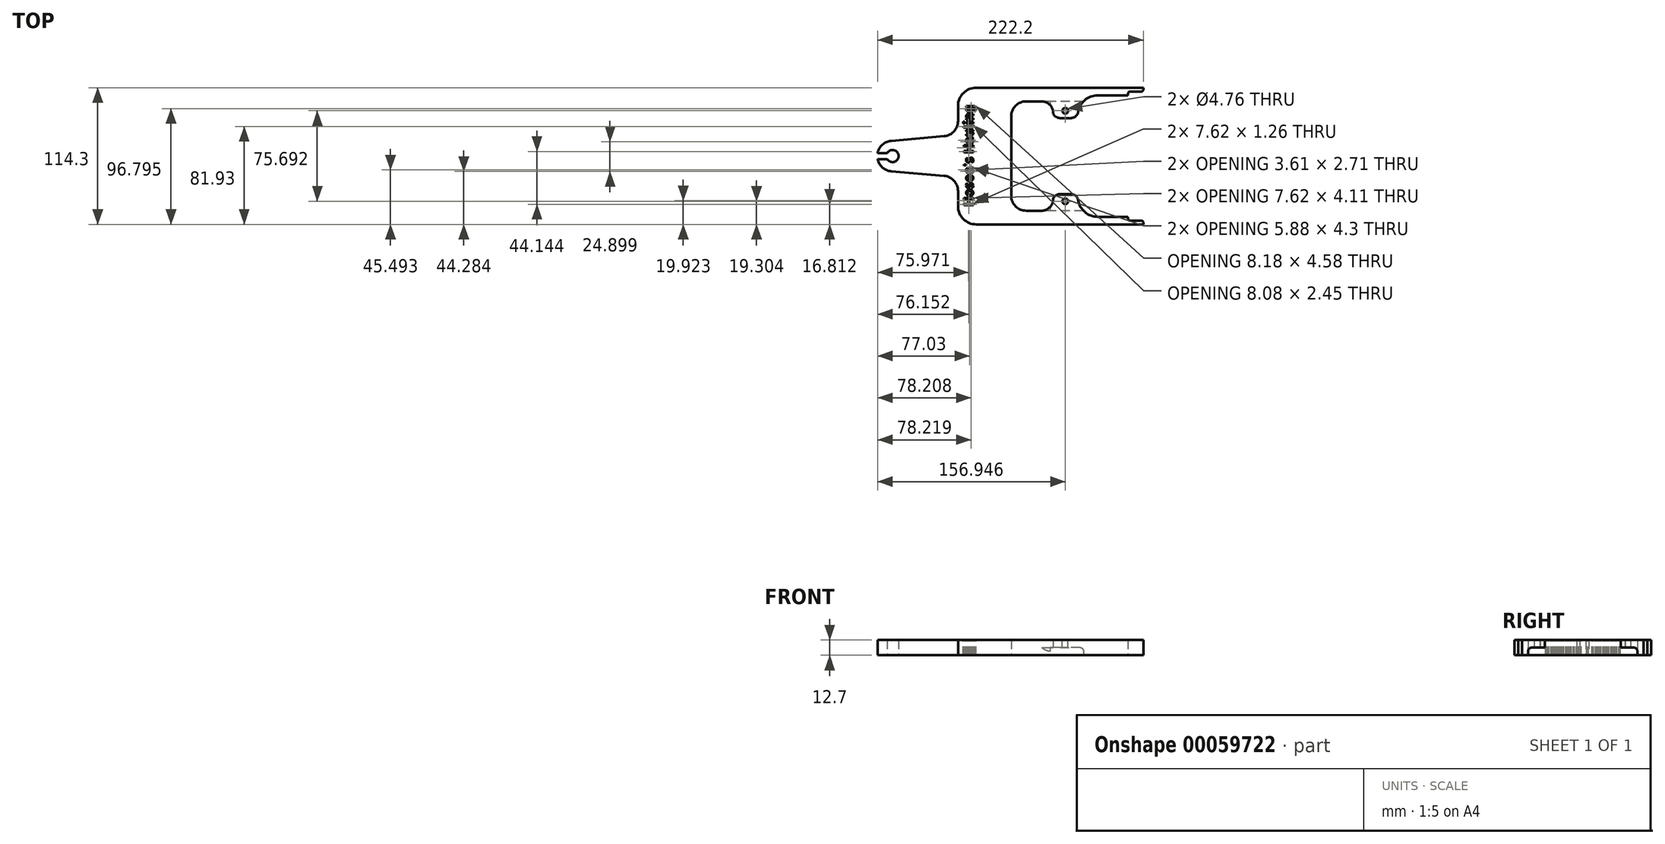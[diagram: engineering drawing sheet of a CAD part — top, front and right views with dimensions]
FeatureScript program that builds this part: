
annotation { "Feature Type Name" : "Feature", "Feature Type Description" : "" }
export const myFeature = defineFeature(function(context is Context, id is Id, definition is map)
    precondition{}
    {
        {
            var Q0;
            Q0=qCreatedBy(makeId("Top.planeOp"),FACE);
            var sketch = newSketch(context, id + "F0", { "sketchPlane" : qUnion([Q0])});
            skLineSegment(sketch, "E0", {"start": v(-226.79, 0) * mm, "end": v(91.5, 0) * mm, "construction": true});
            skLineSegment(sketch, "E1.MirrorCS", {"start": v(-31.43, 31.75) * mm, "end": v(-22.54, 31.75) * mm});
            skLineSegment(sketch, "E2", {"start": v(-116.84, 41.9) * mm, "end": v(-116.84, 29.23) * mm});
            skLineSegment(sketch, "E3", {"start": v(-128.43, 16.57) * mm, "end": v(-172.71, 12.7) * mm});
            skArc(sketch, "E4", {"start": v(-101.6, 57.15) * mm, "mid": v(-112.38, 52.69) * mm, "end": v(-116.84, 41.9) * mm});
            skArc(sketch, "E5.filletArc", {"start": v(-128.43, 16.57) * mm, "mid": v(-120.18, 20.65) * mm, "end": v(-116.84, 29.23) * mm});
            skArc(sketch, "E6.MirrorCS", {"start": v(-101.6, -57.15) * mm, "mid": v(-112.38, -52.69) * mm, "end": v(-116.84, -41.9) * mm});
            skLineSegment(sketch, "E7.MirrorCS", {"start": v(-116.84, -41.9) * mm, "end": v(-116.84, -29.23) * mm});
            skArc(sketch, "E8.MirrorCS", {"start": v(-128.43, -16.57) * mm, "mid": v(-120.18, -20.65) * mm, "end": v(-116.84, -29.23) * mm});
            skLineSegment(sketch, "E9.MirrorCS", {"start": v(-128.43, -16.57) * mm, "end": v(-172.71, -12.7) * mm});
            skArc(sketch, "E10", {"start": v(-172.71, 12.7) * mm, "mid": v(-180.1, 9.51) * mm, "end": v(-184.1, 2.54) * mm});
            skArc(sketch, "E11.filletArc", {"start": v(-37.25, 35.56) * mm, "mid": v(-34.9, 32.79) * mm, "end": v(-31.43, 31.75) * mm});
            skArc(sketch, "E12.filletArc", {"start": v(-22.54, 31.75) * mm, "mid": v(-18.44, 33.25) * mm, "end": v(-16.28, 37.04) * mm});
            skArc(sketch, "E13", {"start": v(0, 50.8) * mm, "mid": v(-10.66, 46.9) * mm, "end": v(-16.28, 37.04) * mm});
            skLineSegment(sketch, "E14", {"start": v(-101.6, 57.15) * mm, "end": v(38.1, 57.15) * mm});
            skLineSegment(sketch, "E15", {"start": v(38.1, 57.15) * mm, "end": v(38.1, 55.56) * mm});
            skLineSegment(sketch, "E16", {"start": v(36.51, 53.98) * mm, "end": v(26.99, 53.98) * mm});
            skLineSegment(sketch, "E17", {"start": v(25.4, 52.39) * mm, "end": v(25.4, 50.8) * mm});
            skLineSegment(sketch, "E18", {"start": v(25.4, 50.8) * mm, "end": v(0, 50.8) * mm});
            skPoint(sketch, "E19.visualSharp", {"position": v(25.4, 53.98) * mm});
            skArc(sketch, "E19.filletArc", {"start": v(26.99, 53.98) * mm, "mid": v(25.86, 53.51) * mm, "end": v(25.4, 52.39) * mm});
            skPoint(sketch, "E20.visualSharp", {"position": v(38.1, 53.98) * mm});
            skArc(sketch, "E20.filletArc", {"start": v(36.51, 53.98) * mm, "mid": v(37.64, 54.44) * mm, "end": v(38.1, 55.56) * mm});
            skLineSegment(sketch, "E21", {"start": v(-72.4, 33.02) * mm, "end": v(-72.4, 0) * mm});
            skLineSegment(sketch, "E22", {"start": v(-184.1, 2.54) * mm, "end": v(-176, 2.54) * mm});
            skLineSegment(sketch, "E23", {"start": v(-184.1, -2.54) * mm, "end": v(-176, -2.54) * mm});
            skArc(sketch, "E24", {"start": v(-176, -2.54) * mm, "mid": v(-166.52, 0) * mm, "end": v(-176, 2.54) * mm});
            skArc(sketch, "E25.trimOffspring", {"start": v(-184.1, -2.54) * mm, "mid": v(-180.1, -9.51) * mm, "end": v(-172.71, -12.7) * mm});
            skLineSegment(sketch, "E26", {"start": v(-47, 45.72) * mm, "end": v(-59.7, 45.72) * mm});
            skArc(sketch, "E27", {"start": v(-37.25, 35.56) * mm, "mid": v(-39.95, 42.72) * mm, "end": v(-47, 45.72) * mm});
            skPoint(sketch, "E28.visualSharp", {"position": v(-72.4, 45.72) * mm});
            skArc(sketch, "E28.filletArc", {"start": v(-59.7, 45.72) * mm, "mid": v(-68.67, 42) * mm, "end": v(-72.4, 33.02) * mm});
            skLineSegment(sketch, "E29.MirrorCS", {"start": v(38.1, -57.15) * mm, "end": v(38.1, -55.56) * mm});
            skArc(sketch, "E30.MirrorCS", {"start": v(36.51, -53.98) * mm, "mid": v(37.64, -54.44) * mm, "end": v(38.1, -55.56) * mm});
            skArc(sketch, "E31.MirrorCS", {"start": v(26.99, -53.98) * mm, "mid": v(25.86, -53.51) * mm, "end": v(25.4, -52.39) * mm});
            skLineSegment(sketch, "E32.MirrorCS", {"start": v(25.4, -52.39) * mm, "end": v(25.4, -50.8) * mm});
            skArc(sketch, "E33.MirrorCS", {"start": v(-37.25, -35.56) * mm, "mid": v(-34.9, -32.79) * mm, "end": v(-31.43, -31.75) * mm});
            skPoint(sketch, "E34.MirrorP", {"position": v(38.1, -53.98) * mm});
            skPoint(sketch, "E35.MirrorP", {"position": v(25.4, -53.98) * mm});
            skLineSegment(sketch, "E36.MirrorCS", {"start": v(36.51, -53.98) * mm, "end": v(26.99, -53.98) * mm});
            skLineSegment(sketch, "E37.MirrorCS", {"start": v(-72.4, -33.02) * mm, "end": v(-72.4, 0) * mm});
            skLineSegment(sketch, "E38.MirrorCS", {"start": v(-47, -45.72) * mm, "end": v(-59.7, -45.72) * mm});
            skArc(sketch, "E39.MirrorCS", {"start": v(-22.54, -31.75) * mm, "mid": v(-18.44, -33.25) * mm, "end": v(-16.28, -37.04) * mm});
            skArc(sketch, "E40.MirrorCS", {"start": v(0, -50.8) * mm, "mid": v(-10.66, -46.9) * mm, "end": v(-16.28, -37.04) * mm});
            skArc(sketch, "E41.MirrorCS", {"start": v(-37.25, -35.56) * mm, "mid": v(-39.95, -42.72) * mm, "end": v(-47, -45.72) * mm});
            skLineSegment(sketch, "E42.MirrorCS", {"start": v(25.4, -50.8) * mm, "end": v(0, -50.8) * mm});
            skLineSegment(sketch, "E43.MirrorCS", {"start": v(-101.6, -57.15) * mm, "end": v(38.1, -57.15) * mm});
            skArc(sketch, "E44.MirrorCS", {"start": v(-59.7, -45.72) * mm, "mid": v(-68.67, -42) * mm, "end": v(-72.4, -33.02) * mm});
            skPoint(sketch, "E45.MirrorP", {"position": v(-72.4, -45.72) * mm});
            skLineSegment(sketch, "E46.MirrorCS", {"start": v(-31.43, -31.75) * mm, "end": v(-22.54, -31.75) * mm});
            skSolve(sketch);
        }
        {
            var Q0;
            Q0=makeQuery(id+"F0.imprint","IMPRINT",FACE,{"disambiguationData":[TD([[makeQuery(id+"F0.imprint","IMPRINT",EDGE,{"derivedFrom":sQuery(id+"F0.wireOp",EDGE,"E1.MirrorCS")}),1.0]])]});
            extrude(context, id + "F1", {"entities" : qUnion([Q0]), "depth" : 12.7 * mm});
        }
        {
            var Q0;
            Q0=makeQuery(id+"F1.opExtrude","CAP_FACE",FACE,{"disambiguationData":[OSD([sQuery(id+"F0.wireOp",EDGE,"E1.MirrorCS"),sQuery(id+"F0.wireOp",EDGE,"E2"),sQuery(id+"F0.wireOp",EDGE,"E3"),sQuery(id+"F0.wireOp",EDGE,"E4"),sQuery(id+"F0.wireOp",EDGE,"E5.filletArc"),sQuery(id+"F0.wireOp",EDGE,"E7.MirrorCS"),sQuery(id+"F0.wireOp",EDGE,"E8.MirrorCS"),sQuery(id+"F0.wireOp",EDGE,"E9.MirrorCS"),sQuery(id+"F0.wireOp",EDGE,"E10"),sQuery(id+"F0.wireOp",EDGE,"ed6b8572-d190-4678-89e8-abdbb25ba1cc"),sQuery(id+"F0.wireOp",EDGE,"E11.filletArc"),sQuery(id+"F0.wireOp",EDGE,"E12.filletArc"),sQuery(id+"F0.wireOp",EDGE,"E13"),sQuery(id+"F0.wireOp",EDGE,"E14"),sQuery(id+"F0.wireOp",EDGE,"E15"),sQuery(id+"F0.wireOp",EDGE,"E16"),sQuery(id+"F0.wireOp",EDGE,"E17"),sQuery(id+"F0.wireOp",EDGE,"E18"),sQuery(id+"F0.wireOp",EDGE,"E19.filletArc"),sQuery(id+"F0.wireOp",EDGE,"E20.filletArc"),sQuery(id+"F0.wireOp",EDGE,"E21"),sQuery(id+"F0.wireOp",EDGE,"bec62c27-19f1-4f1e-baea-a3420ca4f23a0.MirrorCS"),sQuery(id+"F0.wireOp",EDGE,"bec62c27-19f1-4f1e-baea-a3420ca4f23a1.MirrorCS"),sQuery(id+"F0.wireOp",EDGE,"bec62c27-19f1-4f1e-baea-a3420ca4f23a2.MirrorCS"),sQuery(id+"F0.wireOp",EDGE,"bec62c27-19f1-4f1e-baea-a3420ca4f23a3.MirrorCS"),sQuery(id+"F0.wireOp",EDGE,"bec62c27-19f1-4f1e-baea-a3420ca4f23a4.MirrorCS"),sQuery(id+"F0.wireOp",EDGE,"E6.MirrorCS"),sQuery(id+"F0.wireOp",EDGE,"bec62c27-19f1-4f1e-baea-a3420ca4f23a7.MirrorCS"),sQuery(id+"F0.wireOp",EDGE,"bec62c27-19f1-4f1e-baea-a3420ca4f23a8.MirrorCS"),sQuery(id+"F0.wireOp",EDGE,"bec62c27-19f1-4f1e-baea-a3420ca4f23a9.MirrorCS"),sQuery(id+"F0.wireOp",EDGE,"bec62c27-19f1-4f1e-baea-a3420ca4f23a10.MirrorCS"),sQuery(id+"F0.wireOp",EDGE,"bec62c27-19f1-4f1e-baea-a3420ca4f23a11.MirrorCS"),sQuery(id+"F0.wireOp",EDGE,"bec62c27-19f1-4f1e-baea-a3420ca4f23a12.MirrorCS"),sQuery(id+"F0.wireOp",EDGE,"bec62c27-19f1-4f1e-baea-a3420ca4f23a14.MirrorCS"),sQuery(id+"F0.wireOp",EDGE,"bec62c27-19f1-4f1e-baea-a3420ca4f23a15.MirrorCS"),sQuery(id+"F0.wireOp",EDGE,"E22"),sQuery(id+"F0.wireOp",EDGE,"E23"),sQuery(id+"F0.wireOp",EDGE,"E24"),sQuery(id+"F0.wireOp",EDGE,"E25.trimOffspring")])],"isStart":true});
            var sketch = newSketch(context, id + "F2", { "sketchPlane" : qUnion([Q0])});
            skLineSegment(sketch, "E47", {"start": v(-11.91, 45.72) * mm, "end": v(-47, 45.72) * mm});
            skArc(sketch, "E48", {"start": v(-37.72, 38.98) * mm, "mid": v(-41.26, 43.86) * mm, "end": v(-47, 45.72) * mm});
            skArc(sketch, "E49", {"start": v(-37.72, 38.98) * mm, "mid": v(-36.22, 33.93) * mm, "end": v(-31.43, 31.75) * mm});
            skArc(sketch, "E50", {"start": v(-22.54, 31.75) * mm, "mid": v(-18.44, 33.25) * mm, "end": v(-16.28, 37.04) * mm});
            skArc(sketch, "E51", {"start": v(-11.91, 45.72) * mm, "mid": v(-14.75, 41.7) * mm, "end": v(-16.28, 37.04) * mm});
            skLineSegment(sketch, "E52", {"start": v(-31.43, 31.75) * mm, "end": v(-22.54, 31.75) * mm});
            skArc(sketch, "E53.MirrorCS", {"start": v(-11.91, -45.72) * mm, "mid": v(-14.75, -41.7) * mm, "end": v(-16.28, -37.04) * mm});
            skArc(sketch, "E54.MirrorCS", {"start": v(-22.54, -31.75) * mm, "mid": v(-18.44, -33.25) * mm, "end": v(-16.28, -37.04) * mm});
            skArc(sketch, "E55.MirrorCS", {"start": v(-37.72, -38.98) * mm, "mid": v(-36.22, -33.93) * mm, "end": v(-31.43, -31.75) * mm});
            skLineSegment(sketch, "E56.MirrorCS", {"start": v(-31.43, -31.75) * mm, "end": v(-22.54, -31.75) * mm});
            skArc(sketch, "E57.MirrorCS", {"start": v(-37.72, -38.98) * mm, "mid": v(-41.26, -43.86) * mm, "end": v(-47, -45.72) * mm});
            skLineSegment(sketch, "E58.MirrorCS", {"start": v(-11.91, -45.72) * mm, "end": v(-47, -45.72) * mm});
            skSolve(sketch);
        }
        {
            var Q0;
            Q0=makeQuery(id+"F2.imprint","IMPRINT",FACE,{"disambiguationData":[TD([[makeQuery(id+"F2.imprint","IMPRINT",EDGE,{"derivedFrom":sQuery(id+"F2.wireOp",EDGE,"af0a2057-df30-47e2-a675-5637fe0cc87f.bottom")}),-1.0]])]});
            var Q1;
            Q1=makeQuery(id+"F2.imprint","IMPRINT",FACE,{"disambiguationData":[TD([[makeQuery(id+"F2.imprint","IMPRINT",EDGE,{"derivedFrom":sQuery(id+"F2.wireOp",EDGE,"E47")}),1.0]])]});
            var Q2;
            Q2=makeQuery(id+"F2.imprint","IMPRINT",FACE,{"disambiguationData":[TD([[makeQuery(id+"F2.imprint","IMPRINT",EDGE,{"derivedFrom":sQuery(id+"F2.wireOp",EDGE,"E53.MirrorCS")}),1.0]])]});
            var Q3;
            Q3=makeQuery(id+"F2.imprint","IMPRINT",FACE,{"disambiguationData":[TD([[makeQuery(id+"F2.imprint","IMPRINT",EDGE,{"derivedFrom":sQuery(id+"F2.wireOp",EDGE,"e4b41d12-f8e3-4b11-9a8e-5cf74899601c0.MirrorCS")}),-1.0]])]});
            extrude(context, id + "F3", {"entities" : qUnion([Q0, Q1, Q2, Q3]), "operationType" : NewBodyOperationType.REMOVE, "oppositeDirection" : true, "depth" : 6.35 * mm});
        }
        {
            var Q0;
            Q0=makeQuery(id+"F3.boolean.opBoolean","COPY",FACE,{"derivedFrom":makeQuery(id+"F3.opExtrude","CAP_FACE",FACE,{"disambiguationData":[OSD([sQuery(id+"F2.wireOp",EDGE,"E47"),sQuery(id+"F2.wireOp",EDGE,"E48"),sQuery(id+"F2.wireOp",EDGE,"E49"),sQuery(id+"F2.wireOp",EDGE,"E50"),sQuery(id+"F2.wireOp",EDGE,"E51"),sQuery(id+"F2.wireOp",EDGE,"E52")])],"isStart":false})});
            var sketch = newSketch(context, id + "F4", { "sketchPlane" : qUnion([Q0])});
            skPoint(sketch, "E59", {"position": v(-27.15, 37.85) * mm});
            skPoint(sketch, "E60.MirrorP", {"position": v(-27.15, -37.85) * mm});
            skSolve(sketch);
        }
        {
            var Q0;
            Q0=sQuery(id+"F4.wireOp",VERTEX,"E59");
            var Q1;
            Q1=sQuery(id+"F4.wireOp",VERTEX,"E60.MirrorP");
            var Q2;
            Q2=makeQuery(id+"F1.opExtrude","SWEPT_BODY",BODY,{"disambiguationData":[OSD([sQuery(id+"F0.wireOp",EDGE,"E1.MirrorCS"),sQuery(id+"F0.wireOp",EDGE,"E2"),sQuery(id+"F0.wireOp",EDGE,"E3"),sQuery(id+"F0.wireOp",EDGE,"E4"),sQuery(id+"F0.wireOp",EDGE,"E5.filletArc"),sQuery(id+"F0.wireOp",EDGE,"E7.MirrorCS"),sQuery(id+"F0.wireOp",EDGE,"E8.MirrorCS"),sQuery(id+"F0.wireOp",EDGE,"E9.MirrorCS"),sQuery(id+"F0.wireOp",EDGE,"E10"),sQuery(id+"F0.wireOp",EDGE,"ed6b8572-d190-4678-89e8-abdbb25ba1cc"),sQuery(id+"F0.wireOp",EDGE,"E11.filletArc"),sQuery(id+"F0.wireOp",EDGE,"E12.filletArc"),sQuery(id+"F0.wireOp",EDGE,"E13"),sQuery(id+"F0.wireOp",EDGE,"E14"),sQuery(id+"F0.wireOp",EDGE,"E15"),sQuery(id+"F0.wireOp",EDGE,"E16"),sQuery(id+"F0.wireOp",EDGE,"E17"),sQuery(id+"F0.wireOp",EDGE,"E18"),sQuery(id+"F0.wireOp",EDGE,"E19.filletArc"),sQuery(id+"F0.wireOp",EDGE,"E20.filletArc"),sQuery(id+"F0.wireOp",EDGE,"E21"),sQuery(id+"F0.wireOp",EDGE,"bec62c27-19f1-4f1e-baea-a3420ca4f23a0.MirrorCS"),sQuery(id+"F0.wireOp",EDGE,"bec62c27-19f1-4f1e-baea-a3420ca4f23a1.MirrorCS"),sQuery(id+"F0.wireOp",EDGE,"bec62c27-19f1-4f1e-baea-a3420ca4f23a2.MirrorCS"),sQuery(id+"F0.wireOp",EDGE,"bec62c27-19f1-4f1e-baea-a3420ca4f23a3.MirrorCS"),sQuery(id+"F0.wireOp",EDGE,"bec62c27-19f1-4f1e-baea-a3420ca4f23a4.MirrorCS"),sQuery(id+"F0.wireOp",EDGE,"E6.MirrorCS"),sQuery(id+"F0.wireOp",EDGE,"bec62c27-19f1-4f1e-baea-a3420ca4f23a7.MirrorCS"),sQuery(id+"F0.wireOp",EDGE,"bec62c27-19f1-4f1e-baea-a3420ca4f23a8.MirrorCS"),sQuery(id+"F0.wireOp",EDGE,"bec62c27-19f1-4f1e-baea-a3420ca4f23a9.MirrorCS"),sQuery(id+"F0.wireOp",EDGE,"bec62c27-19f1-4f1e-baea-a3420ca4f23a10.MirrorCS"),sQuery(id+"F0.wireOp",EDGE,"bec62c27-19f1-4f1e-baea-a3420ca4f23a11.MirrorCS"),sQuery(id+"F0.wireOp",EDGE,"bec62c27-19f1-4f1e-baea-a3420ca4f23a12.MirrorCS"),sQuery(id+"F0.wireOp",EDGE,"bec62c27-19f1-4f1e-baea-a3420ca4f23a14.MirrorCS"),sQuery(id+"F0.wireOp",EDGE,"bec62c27-19f1-4f1e-baea-a3420ca4f23a15.MirrorCS"),sQuery(id+"F0.wireOp",EDGE,"E22"),sQuery(id+"F0.wireOp",EDGE,"E23"),sQuery(id+"F0.wireOp",EDGE,"E24"),sQuery(id+"F0.wireOp",EDGE,"E25.trimOffspring")])]});
            hole(context, id + "F5", {"style" : HoleStyle.SIMPLE, "holeDiameter" : 4.76 * mm, "endStyle" : HoleEndStyle.THROUGH, "locations" : qUnion([Q0, Q1]), "scope" : qUnion([Q2])});
        }
        {
            var Q0;
            Q0=makeQuery(id+"F1.opExtrude","CAP_FACE",FACE,{"disambiguationData":[OSD([sQuery(id+"F0.wireOp",EDGE,"E1.MirrorCS"),sQuery(id+"F0.wireOp",EDGE,"E2"),sQuery(id+"F0.wireOp",EDGE,"E3"),sQuery(id+"F0.wireOp",EDGE,"E4"),sQuery(id+"F0.wireOp",EDGE,"E5.filletArc"),sQuery(id+"F0.wireOp",EDGE,"E7.MirrorCS"),sQuery(id+"F0.wireOp",EDGE,"E8.MirrorCS"),sQuery(id+"F0.wireOp",EDGE,"E9.MirrorCS"),sQuery(id+"F0.wireOp",EDGE,"E10"),sQuery(id+"F0.wireOp",EDGE,"ed6b8572-d190-4678-89e8-abdbb25ba1cc"),sQuery(id+"F0.wireOp",EDGE,"E11.filletArc"),sQuery(id+"F0.wireOp",EDGE,"E12.filletArc"),sQuery(id+"F0.wireOp",EDGE,"E13"),sQuery(id+"F0.wireOp",EDGE,"E14"),sQuery(id+"F0.wireOp",EDGE,"E15"),sQuery(id+"F0.wireOp",EDGE,"E16"),sQuery(id+"F0.wireOp",EDGE,"E17"),sQuery(id+"F0.wireOp",EDGE,"E18"),sQuery(id+"F0.wireOp",EDGE,"E19.filletArc"),sQuery(id+"F0.wireOp",EDGE,"E20.filletArc"),sQuery(id+"F0.wireOp",EDGE,"E21"),sQuery(id+"F0.wireOp",EDGE,"bec62c27-19f1-4f1e-baea-a3420ca4f23a0.MirrorCS"),sQuery(id+"F0.wireOp",EDGE,"bec62c27-19f1-4f1e-baea-a3420ca4f23a1.MirrorCS"),sQuery(id+"F0.wireOp",EDGE,"bec62c27-19f1-4f1e-baea-a3420ca4f23a2.MirrorCS"),sQuery(id+"F0.wireOp",EDGE,"bec62c27-19f1-4f1e-baea-a3420ca4f23a3.MirrorCS"),sQuery(id+"F0.wireOp",EDGE,"bec62c27-19f1-4f1e-baea-a3420ca4f23a4.MirrorCS"),sQuery(id+"F0.wireOp",EDGE,"E6.MirrorCS"),sQuery(id+"F0.wireOp",EDGE,"bec62c27-19f1-4f1e-baea-a3420ca4f23a7.MirrorCS"),sQuery(id+"F0.wireOp",EDGE,"bec62c27-19f1-4f1e-baea-a3420ca4f23a8.MirrorCS"),sQuery(id+"F0.wireOp",EDGE,"bec62c27-19f1-4f1e-baea-a3420ca4f23a9.MirrorCS"),sQuery(id+"F0.wireOp",EDGE,"bec62c27-19f1-4f1e-baea-a3420ca4f23a10.MirrorCS"),sQuery(id+"F0.wireOp",EDGE,"bec62c27-19f1-4f1e-baea-a3420ca4f23a11.MirrorCS"),sQuery(id+"F0.wireOp",EDGE,"bec62c27-19f1-4f1e-baea-a3420ca4f23a12.MirrorCS"),sQuery(id+"F0.wireOp",EDGE,"bec62c27-19f1-4f1e-baea-a3420ca4f23a14.MirrorCS"),sQuery(id+"F0.wireOp",EDGE,"bec62c27-19f1-4f1e-baea-a3420ca4f23a15.MirrorCS"),sQuery(id+"F0.wireOp",EDGE,"E22"),sQuery(id+"F0.wireOp",EDGE,"E23"),sQuery(id+"F0.wireOp",EDGE,"E24"),sQuery(id+"F0.wireOp",EDGE,"E25.trimOffspring")])],"isStart":false});
            var sketch = newSketch(context, id + "F6", { "sketchPlane" : qUnion([Q0])});
            skText(sketch, "E61", { "text": "Hosea\'s Hauling", "fontName": "AllertaStencil-Regular.ttf"});
            const initialGuessF6  = {"E61": [-0.10414, -0.04194, 0, 1, 0.00762]};
            skSetInitialGuess(sketch, initialGuessF6);
            skSolve(sketch);
        }
        {
            var Q0;
            Q0 = qSketchRegion(id + "F6", true);
            var Q1;
            Q1=makeQuery(id+"F1.opExtrude","CAP_FACE",FACE,{"disambiguationData":[OSD([sQuery(id+"F0.wireOp",EDGE,"E1.MirrorCS"),sQuery(id+"F0.wireOp",EDGE,"E2"),sQuery(id+"F0.wireOp",EDGE,"E3"),sQuery(id+"F0.wireOp",EDGE,"E4"),sQuery(id+"F0.wireOp",EDGE,"E5.filletArc"),sQuery(id+"F0.wireOp",EDGE,"E7.MirrorCS"),sQuery(id+"F0.wireOp",EDGE,"E8.MirrorCS"),sQuery(id+"F0.wireOp",EDGE,"E9.MirrorCS"),sQuery(id+"F0.wireOp",EDGE,"E10"),sQuery(id+"F0.wireOp",EDGE,"ed6b8572-d190-4678-89e8-abdbb25ba1cc"),sQuery(id+"F0.wireOp",EDGE,"E11.filletArc"),sQuery(id+"F0.wireOp",EDGE,"E12.filletArc"),sQuery(id+"F0.wireOp",EDGE,"E13"),sQuery(id+"F0.wireOp",EDGE,"E14"),sQuery(id+"F0.wireOp",EDGE,"E15"),sQuery(id+"F0.wireOp",EDGE,"E16"),sQuery(id+"F0.wireOp",EDGE,"E17"),sQuery(id+"F0.wireOp",EDGE,"E18"),sQuery(id+"F0.wireOp",EDGE,"E19.filletArc"),sQuery(id+"F0.wireOp",EDGE,"E20.filletArc"),sQuery(id+"F0.wireOp",EDGE,"E21"),sQuery(id+"F0.wireOp",EDGE,"bec62c27-19f1-4f1e-baea-a3420ca4f23a0.MirrorCS"),sQuery(id+"F0.wireOp",EDGE,"bec62c27-19f1-4f1e-baea-a3420ca4f23a1.MirrorCS"),sQuery(id+"F0.wireOp",EDGE,"bec62c27-19f1-4f1e-baea-a3420ca4f23a2.MirrorCS"),sQuery(id+"F0.wireOp",EDGE,"bec62c27-19f1-4f1e-baea-a3420ca4f23a3.MirrorCS"),sQuery(id+"F0.wireOp",EDGE,"bec62c27-19f1-4f1e-baea-a3420ca4f23a4.MirrorCS"),sQuery(id+"F0.wireOp",EDGE,"E6.MirrorCS"),sQuery(id+"F0.wireOp",EDGE,"bec62c27-19f1-4f1e-baea-a3420ca4f23a7.MirrorCS"),sQuery(id+"F0.wireOp",EDGE,"bec62c27-19f1-4f1e-baea-a3420ca4f23a8.MirrorCS"),sQuery(id+"F0.wireOp",EDGE,"bec62c27-19f1-4f1e-baea-a3420ca4f23a9.MirrorCS"),sQuery(id+"F0.wireOp",EDGE,"bec62c27-19f1-4f1e-baea-a3420ca4f23a10.MirrorCS"),sQuery(id+"F0.wireOp",EDGE,"bec62c27-19f1-4f1e-baea-a3420ca4f23a11.MirrorCS"),sQuery(id+"F0.wireOp",EDGE,"bec62c27-19f1-4f1e-baea-a3420ca4f23a12.MirrorCS"),sQuery(id+"F0.wireOp",EDGE,"bec62c27-19f1-4f1e-baea-a3420ca4f23a14.MirrorCS"),sQuery(id+"F0.wireOp",EDGE,"bec62c27-19f1-4f1e-baea-a3420ca4f23a15.MirrorCS"),sQuery(id+"F0.wireOp",EDGE,"E22"),sQuery(id+"F0.wireOp",EDGE,"E23"),sQuery(id+"F0.wireOp",EDGE,"E24"),sQuery(id+"F0.wireOp",EDGE,"E25.trimOffspring")])],"isStart":true});
            extrude(context, id + "F7", {"entities" : qUnion([Q0]), "operationType" : NewBodyOperationType.REMOVE, "endBound" : BoundingType.UP_TO_SURFACE, "oppositeDirection" : true, "endBoundEntityFace" : qUnion([Q1]), "depth" : 25.4 * mm});
        }
        {
            var Q0;
            Q0=makeQuery(id+"F3.boolean.opBoolean","COPY",EDGE,{"derivedFrom":makeQuery(id+"F3.opExtrude","CAP_EDGE",EDGE,{"disambiguationData":[OSD([sQuery(id+"F2.wireOp",EDGE,"E58.MirrorCS")])],"isStart":false})});
            var Q1;
            Q1=makeQuery(id+"F3.boolean.opBoolean","COPY",EDGE,{"derivedFrom":makeQuery(id+"F3.opExtrude","CAP_EDGE",EDGE,{"disambiguationData":[OSD([sQuery(id+"F2.wireOp",EDGE,"E47")])],"isStart":false})});
            fillet(context, id + "F8", {"entities" : qUnion([Q0, Q1]), "radius" : 3.17 * mm, "allowEdgeOverflow" : false});
        }
    });
